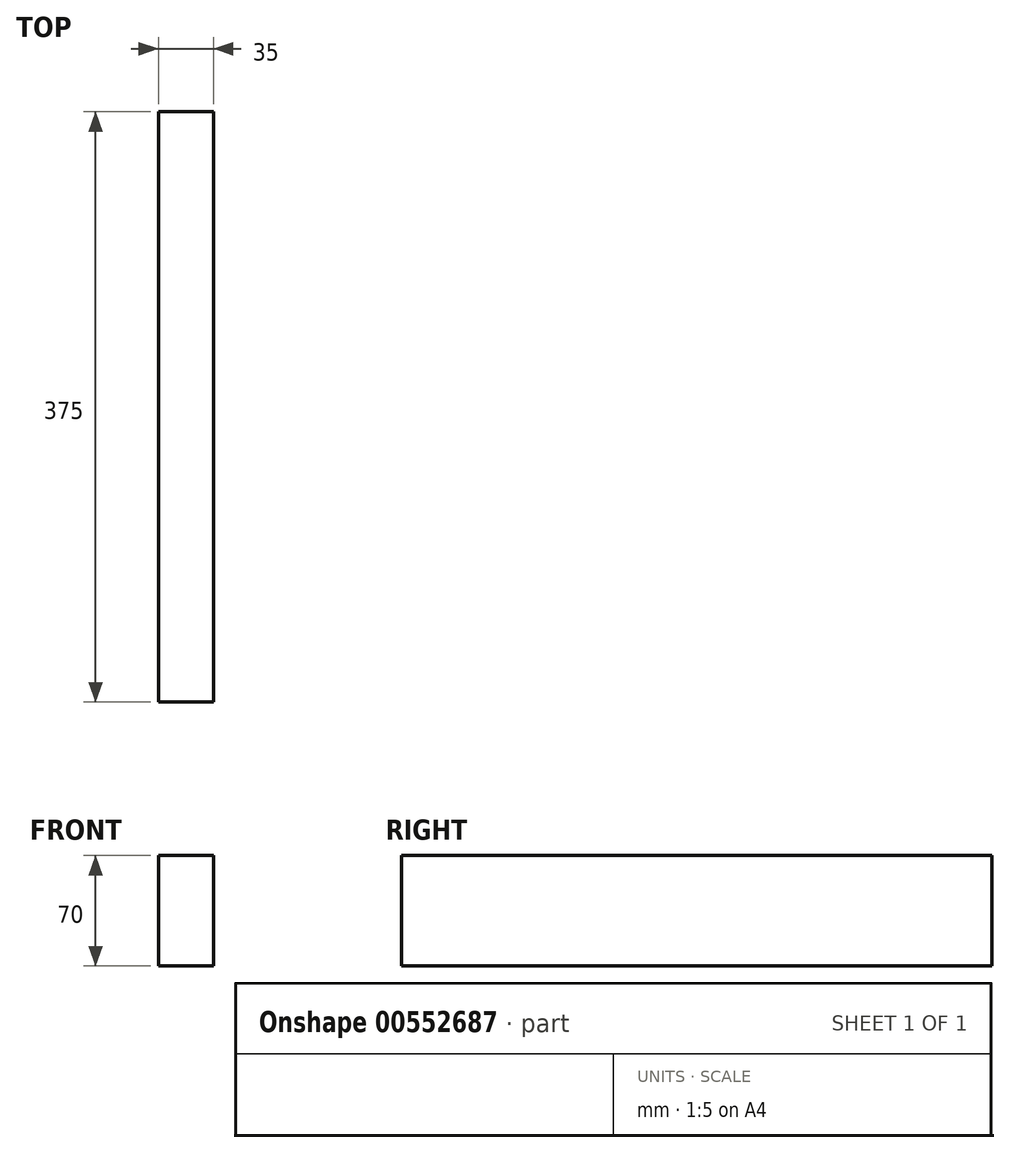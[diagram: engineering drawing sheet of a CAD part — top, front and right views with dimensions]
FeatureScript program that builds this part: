
annotation { "Feature Type Name" : "Feature", "Feature Type Description" : "" }
export const myFeature = defineFeature(function(context is Context, id is Id, definition is map)
    precondition{}
    {
        {
            var Q0;
            Q0=qCreatedBy(makeId("Front.planeOp"),FACE);
            var sketch = newSketch(context, id + "F0", { "sketchPlane" : qUnion([Q0])});
            skLineSegment(sketch, "E0.bottom", {"start": v(17.5, 35) * mm, "end": v(-17.5, 35) * mm});
            skLineSegment(sketch, "E0.top", {"start": v(17.5, -35) * mm, "end": v(-17.5, -35) * mm});
            skLineSegment(sketch, "E0.left", {"start": v(17.5, 35) * mm, "end": v(17.5, -35) * mm});
            skLineSegment(sketch, "E0.right", {"start": v(-17.5, 35) * mm, "end": v(-17.5, -35) * mm});
            skPoint(sketch, "E0.middle", {"position": v(0, 0) * mm});
            skSolve(sketch);
        }
        {
            var Q0;
            Q0 = qSketchRegion(id + "F0", true);
            extrude(context, id + "F1", {"entities" : qUnion([Q0]), "oppositeDirection" : true, "depth" : 375 * mm, "offsetDistance" : 25 * mm});
        }
    });
